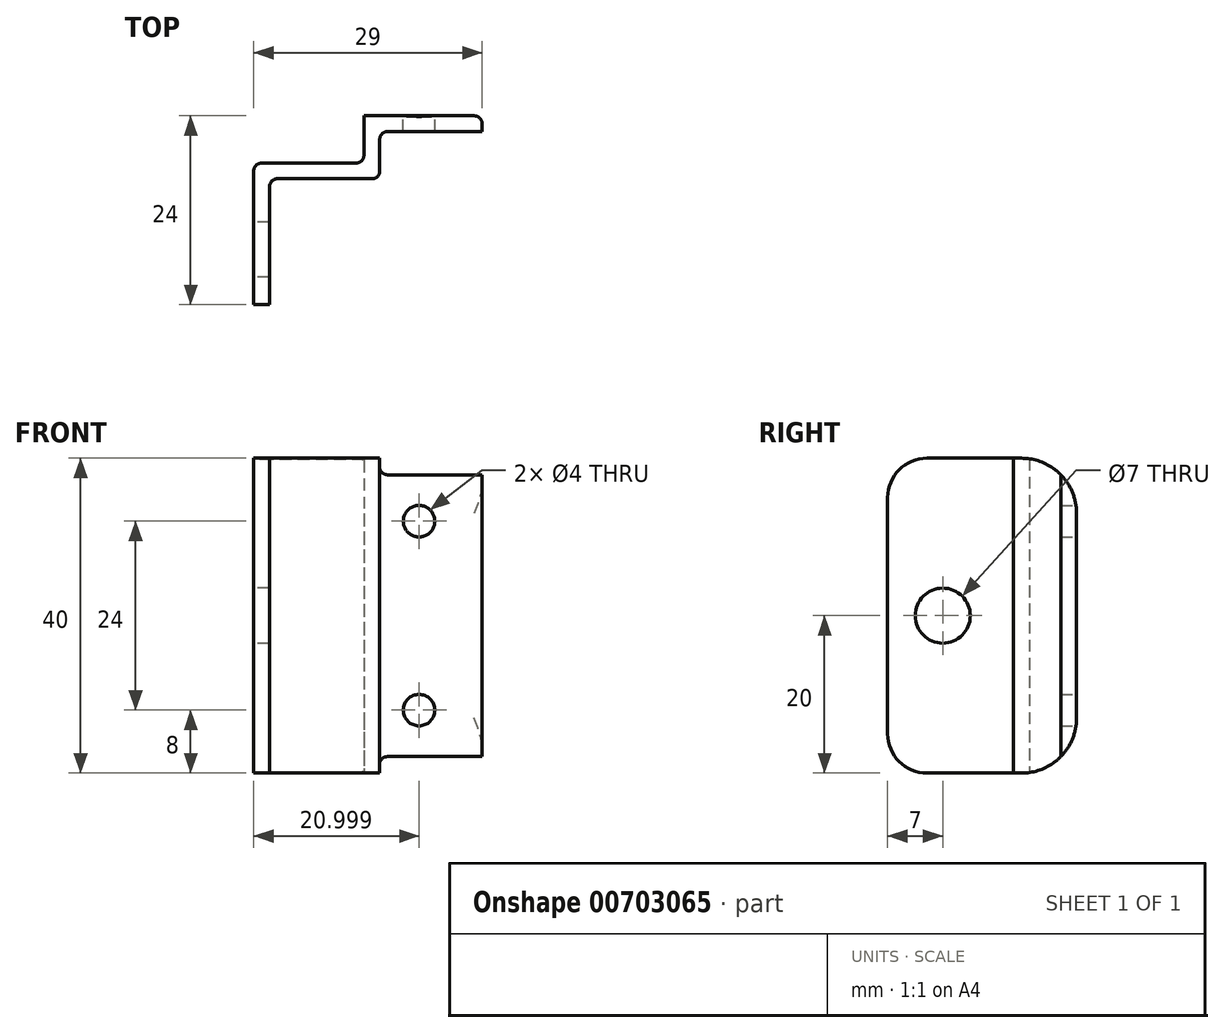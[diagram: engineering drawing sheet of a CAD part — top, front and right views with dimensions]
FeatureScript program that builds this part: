
annotation { "Feature Type Name" : "Feature", "Feature Type Description" : "" }
export const myFeature = defineFeature(function(context is Context, id is Id, definition is map)
    precondition{}
    {
        {
            var Q0;
            Q0=qCreatedBy(makeId("Top.planeOp"),FACE);
            var sketch = newSketch(context, id + "F0", { "sketchPlane" : qUnion([Q0])});
            skLineSegment(sketch, "E0.bottom", {"start": v(-7, 5.99) * mm, "end": v(-5, 5.99) * mm});
            skLineSegment(sketch, "E0.top", {"start": v(-7, -12.01) * mm, "end": v(-5, -12.01) * mm});
            skLineSegment(sketch, "E0.left", {"start": v(-7, 5.99) * mm, "end": v(-7, -12.01) * mm});
            skLineSegment(sketch, "E0.right", {"start": v(-5, 3.99) * mm, "end": v(-5, -12.01) * mm});
            skLineSegment(sketch, "E1.bottom", {"start": v(-5, 5.99) * mm, "end": v(7, 5.99) * mm});
            skLineSegment(sketch, "E1.top", {"start": v(-5, 3.99) * mm, "end": v(7, 3.99) * mm});
            skLineSegment(sketch, "E2.bottom", {"start": v(7, 3.99) * mm, "end": v(9, 3.99) * mm});
            skLineSegment(sketch, "E2.top", {"start": v(7, 11.99) * mm, "end": v(9, 11.99) * mm});
            skLineSegment(sketch, "E2.left", {"start": v(7, 5.99) * mm, "end": v(7, 11.99) * mm});
            skLineSegment(sketch, "E2.right", {"start": v(9, 3.99) * mm, "end": v(9, 9.99) * mm});
            skLineSegment(sketch, "E3.bottom", {"start": v(7, 11.99) * mm, "end": v(22, 11.99) * mm});
            skLineSegment(sketch, "E3.top", {"start": v(9, 9.99) * mm, "end": v(22, 9.99) * mm});
            skLineSegment(sketch, "E3.left", {"start": v(7, 11.99) * mm, "end": v(7, 9.99) * mm});
            skLineSegment(sketch, "E3.right", {"start": v(22, 11.99) * mm, "end": v(22, 9.99) * mm});
            skSolve(sketch);
        }
        {
            var Q0;
            Q0 = qSketchRegion(id + "F0", true);
            extrude(context, id + "F1", {"entities" : qUnion([Q0]), "depth" : 40 * mm, "offsetDistance" : 25 * mm});
        }
        {
            var Q0;
            Q0=makeQuery(id+"F1.opExtrude","SWEPT_EDGE",EDGE,{"disambiguationData":[OSD([sQuery(id+"F0.wireOp",EDGE,"E0.bottom"),sQuery(id+"F0.wireOp",EDGE,"E0.left")])]});
            var Q1;
            Q1=makeQuery(id+"F1.opExtrude","SWEPT_EDGE",EDGE,{"disambiguationData":[OSD([sQuery(id+"F0.wireOp",EDGE,"E3.bottom"),sQuery(id+"F0.wireOp",EDGE,"E3.left")])]});
            var Q2;
            Q2=makeQuery(id+"F1.opExtrude","SWEPT_EDGE",EDGE,{"disambiguationData":[OSD([sQuery(id+"F0.wireOp",EDGE,"E0.right"),sQuery(id+"F0.wireOp",EDGE,"E1.top")])]});
            var Q3;
            Q3=makeQuery(id+"F1.opExtrude","SWEPT_EDGE",EDGE,{"disambiguationData":[OSD([sQuery(id+"F0.wireOp",EDGE,"E2.right"),sQuery(id+"F0.wireOp",EDGE,"E3.top")])]});
            var Q4;
            Q4=makeQuery(id+"F1.opExtrude","SWEPT_EDGE",EDGE,{"disambiguationData":[OSD([sQuery(id+"F0.wireOp",EDGE,"E2.bottom"),sQuery(id+"F0.wireOp",EDGE,"E2.right")])]});
            var Q5;
            Q5=makeQuery(id+"F1.opExtrude","SWEPT_EDGE",EDGE,{"disambiguationData":[OSD([sQuery(id+"F0.wireOp",EDGE,"E1.bottom"),sQuery(id+"F0.wireOp",EDGE,"E2.left")])]});
            fillet(context, id + "F2", {"entities" : qUnion([Q0, Q1, Q2, Q3, Q4, Q5]), "radius" : 1 * mm, "tangentPropagation" : true, "allowEdgeOverflow" : false});
        }
        {
            var Q0;
            Q0=makeQuery(id+"F1.opExtrude","CAP_EDGE",EDGE,{"disambiguationData":[OSD([sQuery(id+"F0.wireOp",EDGE,"E0.top")])],"isStart":true});
            var Q1;
            Q1=makeQuery(id+"F1.opExtrude","CAP_EDGE",EDGE,{"disambiguationData":[OSD([sQuery(id+"F0.wireOp",EDGE,"E0.top")])],"isStart":false});
            fillet(context, id + "F3", {"entities" : qUnion([Q0, Q1]), "radius" : 5 * mm, "tangentPropagation" : true, "allowEdgeOverflow" : false});
        }
        {
            var Q0;
            Q0=makeQuery(id+"F1.opExtrude","SWEPT_FACE",FACE,{"disambiguationData":[OSD([sQuery(id+"F0.wireOp",EDGE,"E0.left")])]});
            var sketch = newSketch(context, id + "F4", { "sketchPlane" : qUnion([Q0])});
            skCircle(sketch, "E4", {"center": v(5.01, 20) * mm, "radius": 3.5 * mm});
            skSolve(sketch);
        }
        {
            var Q0;
            Q0=makeQuery(id+"F4.imprint","IMPRINT",FACE,{"disambiguationData":[TD([[makeQuery(id+"F4.imprint","IMPRINT",EDGE,{"derivedFrom":sQuery(id+"F4.wireOp",EDGE,"E4")}),1.0]])]});
            extrude(context, id + "F5", {"entities" : qUnion([Q0]), "operationType" : NewBodyOperationType.REMOVE, "oppositeDirection" : true, "depth" : 25 * mm, "offsetDistance" : 25 * mm});
        }
        {
            var Q0;
            Q0=makeQuery(id+"F1.opExtrude","SWEPT_FACE",FACE,{"disambiguationData":[OSD([sQuery(id+"F0.wireOp",EDGE,"E3.bottom")])]});
            var sketch = newSketch(context, id + "F6", { "sketchPlane" : qUnion([Q0])});
            skCircle(sketch, "E5", {"center": v(-14, 32) * mm, "radius": 2 * mm});
            skCircle(sketch, "E6", {"center": v(-14, 8) * mm, "radius": 2 * mm});
            skSolve(sketch);
        }
        {
            var Q0;
            Q0=makeQuery(id+"F6.imprint","IMPRINT",FACE,{"disambiguationData":[TD([[makeQuery(id+"F6.imprint","IMPRINT",EDGE,{"derivedFrom":sQuery(id+"F6.wireOp",EDGE,"E6")}),1.0]])]});
            var Q1;
            Q1=makeQuery(id+"F6.imprint","IMPRINT",FACE,{"disambiguationData":[TD([[makeQuery(id+"F6.imprint","IMPRINT",EDGE,{"derivedFrom":sQuery(id+"F6.wireOp",EDGE,"E5")}),1.0]])]});
            extrude(context, id + "F7", {"entities" : qUnion([Q0, Q1]), "operationType" : NewBodyOperationType.REMOVE, "oppositeDirection" : true, "depth" : 25 * mm, "offsetDistance" : 25 * mm});
        }
        {
            var Q0;
            Q0=makeQuery(id+"F1.opExtrude","CAP_EDGE",EDGE,{"disambiguationData":[OSD([sQuery(id+"F0.wireOp",EDGE,"E3.right")])],"isStart":true});
            var Q1;
            Q1=makeQuery(id+"F1.opExtrude","CAP_EDGE",EDGE,{"disambiguationData":[OSD([sQuery(id+"F0.wireOp",EDGE,"E3.right")])],"isStart":false});
            fillet(context, id + "F8", {"entities" : qUnion([Q0, Q1]), "radius" : 7 * mm, "tangentPropagation" : true, "allowEdgeOverflow" : false});
        }
    });
